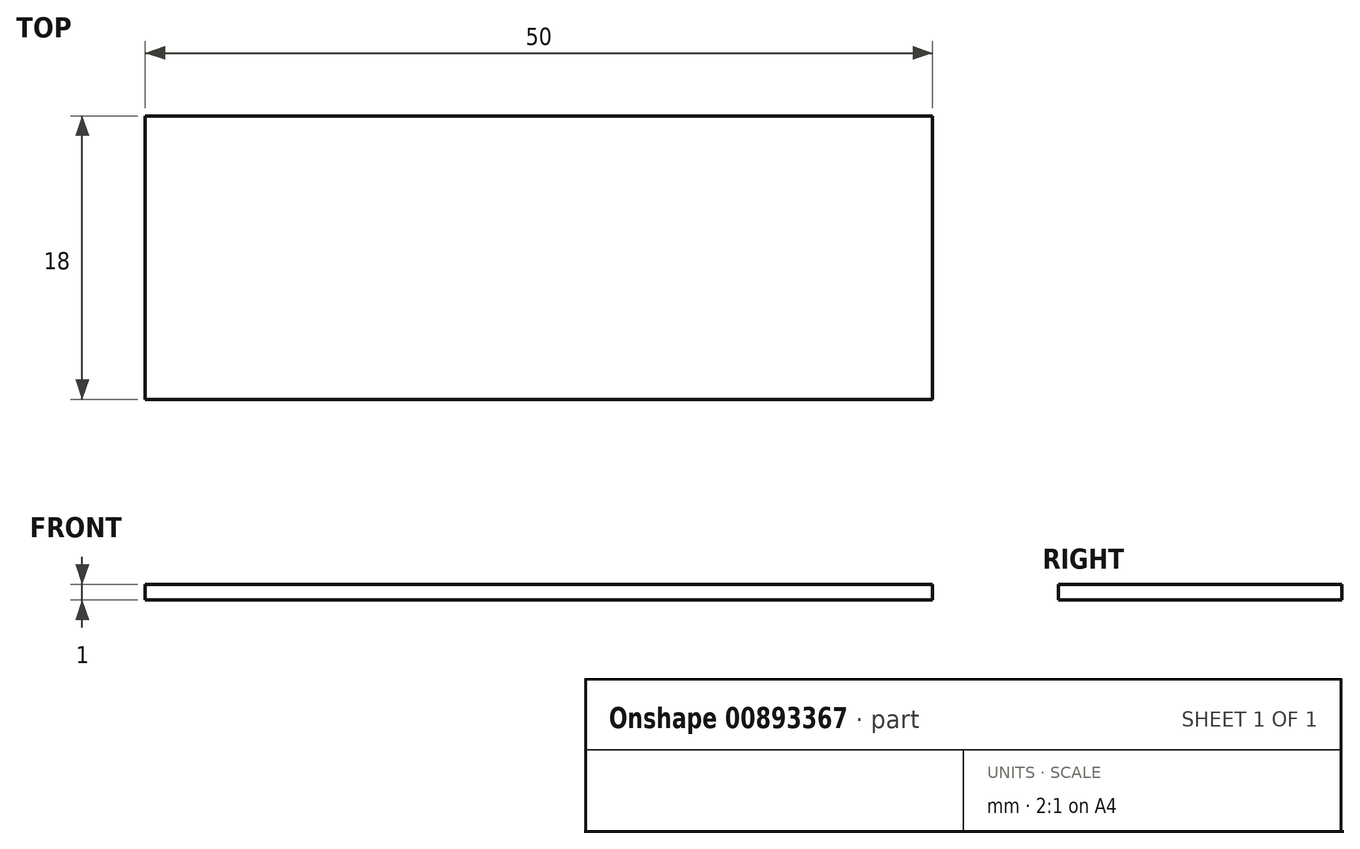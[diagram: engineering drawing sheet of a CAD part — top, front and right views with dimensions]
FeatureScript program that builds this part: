
annotation { "Feature Type Name" : "Feature", "Feature Type Description" : "" }
export const myFeature = defineFeature(function(context is Context, id is Id, definition is map)
    precondition{}
    {
        {
            var Q0;
            Q0=qCreatedBy(makeId("Top.planeOp"),FACE);
            var sketch = newSketch(context, id + "F0", { "sketchPlane" : qUnion([Q0])});
            skLineSegment(sketch, "E0.bottom", {"start": v(25, 9) * mm, "end": v(-25, 9) * mm});
            skLineSegment(sketch, "E0.top", {"start": v(25, -9) * mm, "end": v(-25, -9) * mm});
            skLineSegment(sketch, "E0.left", {"start": v(25, 9) * mm, "end": v(25, -9) * mm});
            skLineSegment(sketch, "E0.right", {"start": v(-25, 9) * mm, "end": v(-25, -9) * mm});
            skPoint(sketch, "E0.middle", {"position": v(0, 0) * mm});
            skSolve(sketch);
        }
        {
            var Q0;
            Q0 = qSketchRegion(id + "F0", true);
            extrude(context, id + "F1", {"entities" : qUnion([Q0]), "depth" : 1 * mm, "offsetDistance" : 25 * mm});
        }
    });
